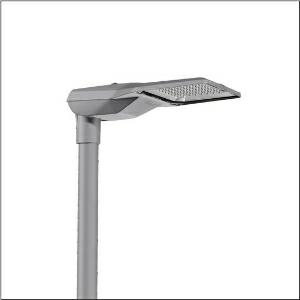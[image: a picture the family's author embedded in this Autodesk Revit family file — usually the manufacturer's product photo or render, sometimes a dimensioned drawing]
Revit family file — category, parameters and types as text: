
# Revit family: streetlight_sl_21_iq_midi___p0_5a_5xe3v31v08mb_f649
name_source: partatom
category: Lighting Fixtures
units: mm (PartAtom-declared; Revit-internal decimal feet)

## family parameters
Cut with Voids When Loaded = No
Host = Face
Light Source = No
Part Type = Normal
Room Calculation Point = No
Round Connector Dimension = Use Diameter
Shared = No

## types (1)
- --- (1 x LED, 18020 lm, 129.3 W, 3000K)
    Apparent Load = 129 VA
    CIE Flux Codes = 37 73 96 100 100
    Color Rendering = 70
    Color Temperature = 3000K
    Default Elevation = 1800 mm
    Description = Streetlight SL 21 iQ midi, mast luminaire, primary light control with lens, of PMMA, primary optical cover: cover, of toughened safety glass, transparent, light distribution: P0.5a, light emission: direct distribution, primary light characteristic: asymmetric, installation type: post-top, side-entry, LED, High Power LED, rated luminous flux: 18.020lm, luminous efficacy: 139lm/W, light colour: 730, colour temperature: 3000K, control gear: iQ-Street Remote, D4i with power reduction, control: pre-setting: logarithmic dimming characteristic, Street-Remote, Auto-Match, Temp-Guard, Lumen-Switch, Night-Set, Smart-Wire, Light-Fading, Desk-Remote (wireless, voltage-free reading and setting of iQ features in the workshop via application-optimized NFC function/RFID function), optimised constant luminous flux control (CLO 2.0), mains connection: 230..240V, AC, 50/60Hz, start of lifetime: 129W, end of service life: 142W, reduction: 56W, luminaire housing, of diecast aluminium, powder-coated, SITECO metallic grey (DB 702S), corrosivity category C5 high according to DIN EN ISO 12944, please order mast flange separately, inclination adjustable: 0°, 5°, 10°, 15°, sealing non-destructively replaceable, multi-level sealing system, length: 644mm, width: 335mm, height: 110mm, mast flange for spigot size: 42mm (side-entry): 5XC10008XM4, 60/48mm (side-entry/post-top): 5XC10108XM2, 76/60mm (side-entry/post-top): 5XC10108XM1, mounting height: 4..8m, Smart Interface above, protection rating (complete): IP66, insulation class (complete): insulation class II (safety insulation), certification: CE, ENEC, ENEC+, VDE, impact resistance: IK10, permissible operating ambient temperature for outdoor applications: -40..+50°C, standard-compliant lighting for roads and squares, packaging unit: 1 piece

Light Distribution: P0.5a
    Height = 111 mm
    Lamp = 1 x LED
    Lamp Light Flux = 18020 lm
    Lamp Power = 129.3 W
    Lamp count = 1
    Length = 644 mm
    Luminous efficacy = 139 lm/W
    Manufacturer = Siteco
    ModVariant = No
    Model = 5XE3V31V08MB
    Number of Poles = 1
    OnlyDefault = Yes
    Power Factor = 1
    Product Name = Streetlight SL 21 iQ midi | P0.5a
    Product group = mast luminaire | pylon top
    ProductGroupID = 6100
    Protection Class = Protection class II
    Protection Degree = IP 66
    RLX_Detail_Level = 1
    RLX_Emergency_Light_Flux = 0 lm
    RLX_Emergency_Type = 0
    RLX_Emergency_Type_DB = No
    RlxData = <blob elided: 90589 chars, md5=24c05df3>
    Socket = socket
    Standby Power = 0 W
    System Light Flux = 18021 lm
    System Power = 129 W
    Type Comments = factory setting: luminous flux: 100 % | dim-lin: 254 | 672 mA
    Type Image = l_1004302.jpg
    URL = http://relux.com
    VarID = @adj_078221
    Voltage = 0 V
    Weight = 0.00 kg
    Width = 336 mm

## geometry (parser evidence)
native form markers: Blend x4, Sweep x12
no freeform markers — native parametric forms only
